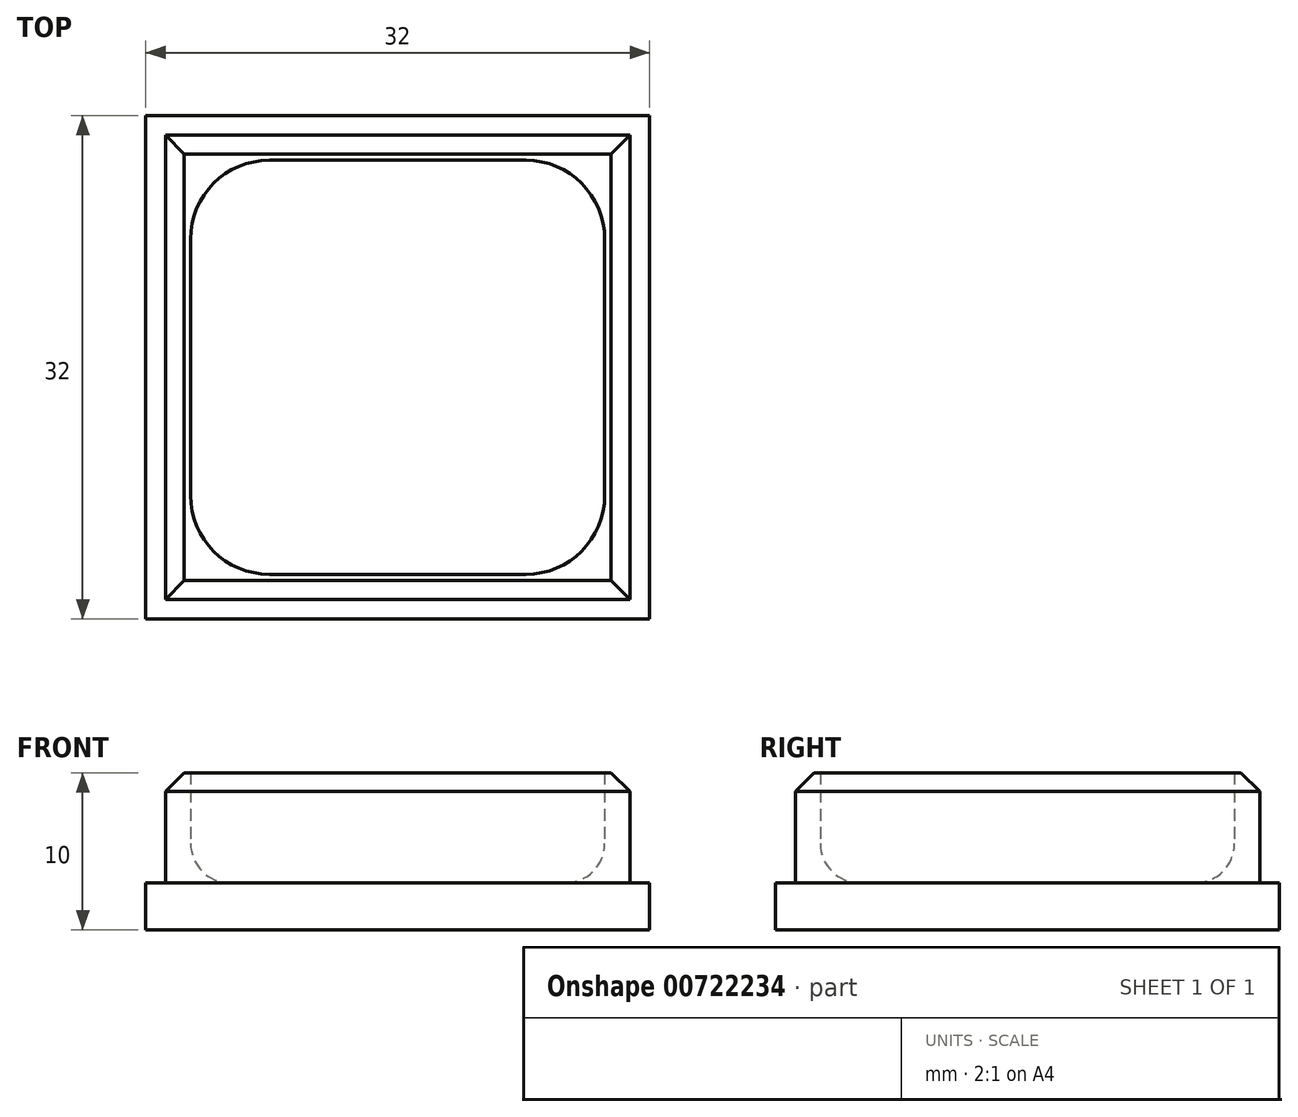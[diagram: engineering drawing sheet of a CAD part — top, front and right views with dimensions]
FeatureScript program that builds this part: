
annotation { "Feature Type Name" : "Feature", "Feature Type Description" : "" }
export const myFeature = defineFeature(function(context is Context, id is Id, definition is map)
    precondition{}
    {
        {
            var Q0;
            Q0=qCreatedBy(makeId("Top.planeOp"),FACE);
            var sketch = newSketch(context, id + "F0", { "sketchPlane" : qUnion([Q0])});
            skLineSegment(sketch, "E0.bottom", {"start": v(16, 16) * mm, "end": v(-16, 16) * mm});
            skLineSegment(sketch, "E0.top", {"start": v(16, -16) * mm, "end": v(-16, -16) * mm});
            skLineSegment(sketch, "E0.left", {"start": v(16, 16) * mm, "end": v(16, -16) * mm});
            skLineSegment(sketch, "E0.right", {"start": v(-16, 16) * mm, "end": v(-16, -16) * mm});
            skPoint(sketch, "E0.middle", {"position": v(0, 0) * mm});
            skLineSegment(sketch, "E1.bottom", {"start": v(14.75, -14.75) * mm, "end": v(-14.75, -14.75) * mm});
            skLineSegment(sketch, "E1.top", {"start": v(14.75, 14.75) * mm, "end": v(-14.75, 14.75) * mm});
            skLineSegment(sketch, "E1.left", {"start": v(14.75, -14.75) * mm, "end": v(14.75, 14.75) * mm});
            skLineSegment(sketch, "E1.right", {"start": v(-14.75, -14.75) * mm, "end": v(-14.75, 14.75) * mm});
            skLineSegment(sketch, "E2.bottom", {"start": v(-13.15, 13.15) * mm, "end": v(13.15, 13.15) * mm});
            skLineSegment(sketch, "E2.top", {"start": v(-13.15, -13.15) * mm, "end": v(13.15, -13.15) * mm});
            skLineSegment(sketch, "E2.left", {"start": v(-13.15, 13.15) * mm, "end": v(-13.15, -13.15) * mm});
            skLineSegment(sketch, "E2.right", {"start": v(13.15, 13.15) * mm, "end": v(13.15, -13.15) * mm});
            skSolve(sketch);
        }
        {
            var Q0;
            Q0=makeQuery(id+"F0.imprint","IMPRINT",FACE,{"disambiguationData":[TD([[makeQuery(id+"F0.imprint","IMPRINT",EDGE,{"derivedFrom":sQuery(id+"F0.wireOp",EDGE,"E0.bottom")}),1.0]])]});
            var Q1;
            Q1=makeQuery(id+"F0.imprint","IMPRINT",FACE,{"disambiguationData":[TD([[makeQuery(id+"F0.imprint","IMPRINT",EDGE,{"derivedFrom":sQuery(id+"F0.wireOp",EDGE,"E1.bottom")}),-1.0]])]});
            var Q2;
            Q2=makeQuery(id+"F0.imprint","IMPRINT",FACE,{"disambiguationData":[TD([[makeQuery(id+"F0.imprint","IMPRINT",EDGE,{"derivedFrom":sQuery(id+"F0.wireOp",EDGE,"E2.bottom")}),-1.0]])]});
            extrude(context, id + "F1", {"entities" : qUnion([Q0, Q1, Q2]), "depth" : 3 * mm, "offsetDistance" : 25 * mm});
        }
        {
            var Q0;
            Q0=makeQuery(id+"F0.imprint","IMPRINT",FACE,{"disambiguationData":[TD([[makeQuery(id+"F0.imprint","IMPRINT",EDGE,{"derivedFrom":sQuery(id+"F0.wireOp",EDGE,"E1.bottom")}),-1.0]])]});
            extrude(context, id + "F2", {"entities" : qUnion([Q0]), "operationType" : NewBodyOperationType.ADD, "depth" : 10 * mm, "offsetDistance" : 25 * mm});
        }
        {
            var Q0;
            Q0=makeQuery(id+"F2.opExtrude","SWEPT_EDGE",EDGE,{"disambiguationData":[OSD([sQuery(id+"F0.wireOp",EDGE,"E2.bottom"),sQuery(id+"F0.wireOp",EDGE,"E2.left")])]});
            var Q1;
            Q1=makeQuery(id+"F2.opExtrude","SWEPT_EDGE",EDGE,{"disambiguationData":[OSD([sQuery(id+"F0.wireOp",EDGE,"E2.bottom"),sQuery(id+"F0.wireOp",EDGE,"E2.right")])]});
            var Q2;
            Q2=makeQuery(id+"F2.opExtrude","SWEPT_EDGE",EDGE,{"disambiguationData":[OSD([sQuery(id+"F0.wireOp",EDGE,"E2.top"),sQuery(id+"F0.wireOp",EDGE,"E2.right")])]});
            var Q3;
            Q3=makeQuery(id+"F2.opExtrude","SWEPT_EDGE",EDGE,{"disambiguationData":[OSD([sQuery(id+"F0.wireOp",EDGE,"E2.top"),sQuery(id+"F0.wireOp",EDGE,"E2.left")])]});
            fillet(context, id + "F3", {"entities" : qUnion([Q0, Q1, Q2, Q3]), "radius" : 5 * mm, "tangentPropagation" : true, "allowEdgeOverflow" : false});
        }
        {
            var Q0;
            Q0=makeQuery(id+"F2.opExtrude","CAP_EDGE",EDGE,{"disambiguationData":[OSD([sQuery(id+"F0.wireOp",EDGE,"E1.right")])],"isStart":false});
            var Q1;
            Q1=makeQuery(id+"F2.opExtrude","CAP_EDGE",EDGE,{"disambiguationData":[OSD([sQuery(id+"F0.wireOp",EDGE,"E1.bottom")])],"isStart":false});
            var Q2;
            Q2=makeQuery(id+"F2.opExtrude","CAP_EDGE",EDGE,{"disambiguationData":[OSD([sQuery(id+"F0.wireOp",EDGE,"E1.top")])],"isStart":false});
            var Q3;
            Q3=makeQuery(id+"F2.opExtrude","CAP_EDGE",EDGE,{"disambiguationData":[OSD([sQuery(id+"F0.wireOp",EDGE,"E1.left")])],"isStart":false});
            chamfer(context, id + "F4", {"entities" : qUnion([Q0, Q1, Q2, Q3]), "width" : 1.2 * mm, "tangentPropagation" : true});
        }
        {
            var Q0;
            {var subQ0=sQuery(id+"F0.wireOp",EDGE,"E2.bottom");var subQ1=sQuery(id+"F0.wireOp",EDGE,"E2.right");Q0=makeQuery(id+"F3.opFillet","BLEND_EDGE",EDGE,{"blendedFrom":[makeQuery(id+"F2.opExtrude","SWEPT_EDGE",EDGE,{"disambiguationData":[OSD([subQ0,subQ1])]}),makeQuery(id+"F2.boolean.opBoolean","SPLIT",FACE,{"disambiguationData":[TD([makeQuery(id+"F2.opExtrude","SWEPT_FACE",FACE,{"disambiguationData":[OSD([subQ0])]})])],"derivedFrom":makeQuery(id+"F1.opExtrude","CAP_FACE",FACE,{"disambiguationData":[OSD([sQuery(id+"F0.wireOp",EDGE,"E0.bottom"),sQuery(id+"F0.wireOp",EDGE,"E0.top"),sQuery(id+"F0.wireOp",EDGE,"E0.left"),sQuery(id+"F0.wireOp",EDGE,"E0.right")])],"isStart":false})})],"blendedInto":[makeQuery(id+"F2.boolean.opBoolean","SPLIT",FACE,{"disambiguationData":[TD([makeQuery(id+"F2.opExtrude","SWEPT_FACE",FACE,{"disambiguationData":[OSD([subQ0])]})])],"derivedFrom":makeQuery(id+"F1.opExtrude","CAP_FACE",FACE,{"disambiguationData":[OSD([sQuery(id+"F0.wireOp",EDGE,"E0.bottom"),sQuery(id+"F0.wireOp",EDGE,"E0.top"),sQuery(id+"F0.wireOp",EDGE,"E0.left"),sQuery(id+"F0.wireOp",EDGE,"E0.right")])],"isStart":false})})]});}
            fillet(context, id + "F5", {"entities" : qUnion([Q0]), "radius" : 2.5 * mm, "tangentPropagation" : true, "allowEdgeOverflow" : false});
        }
    });
